# Revit family: 63_UN_Lightline_WDO SV RS L1250_Norton
name_source: partatom
category: Lighting Fixtures
units: mm (PartAtom-declared; Revit-internal decimal feet)

## family parameters
Always vertical = Yes
Cut with Voids When Loaded = No
Light Source = Yes
OmniClass Number = 23.80.70.11.14.11
OmniClass Title = Downlights
Part Type = Normal
Room Calculation Point = Yes
Round Connector Dimension = Use Diameter
Shared = No
Work Plane-Based = No

## types (1)
- WDOSVRS 84 1 LM2600 1250
    Apparent Load = 22 VA
    Assembly Code = 63.0
    Bracket_Distance = 800 mm  [stored 2.62467 ft]
    Color Filter = 16777215
    Dimming Lamp Color Temperature Shift = <None>
    Emit Shape Visible in Rendering = No
    Emit from Rectangle Length = 101 mm  [stored 0.331365 ft]
    Emit from Rectangle Width = 1242 mm  [stored 4.0748 ft]
    Housing_Material = Laminate, White
    IK Value = IK08
    IP Value = IP66
    IfcExportAs = IfcLightFixtureType
    IfcExportType = USERDEFINED
    Lamp = LED
    Length = 1282 mm  [stored 4.20604 ft]
    Luminous Flux (lm) = 2800 lm
    Manufacturer = Norton
    Model = WDO SV RS
    Photometric Web File = WDOSVRS 84 1 LM2600 1250_LDT.ies
    Tilt Angle = 60.00°
    Type Comments = L1250
    URL = https://www.ivlibrary.com
    Voltage = 230 V
    Wattage Comments = 22W
    calc_length = 1242 mm  [stored 4.0748 ft]

note: [stored X ft] marks values corroborated as IEEE doubles in the binary element streams (Revit-internal decimal feet)

## geometry (parser evidence)
native form markers: Sweep x5
no freeform markers — native parametric forms only
